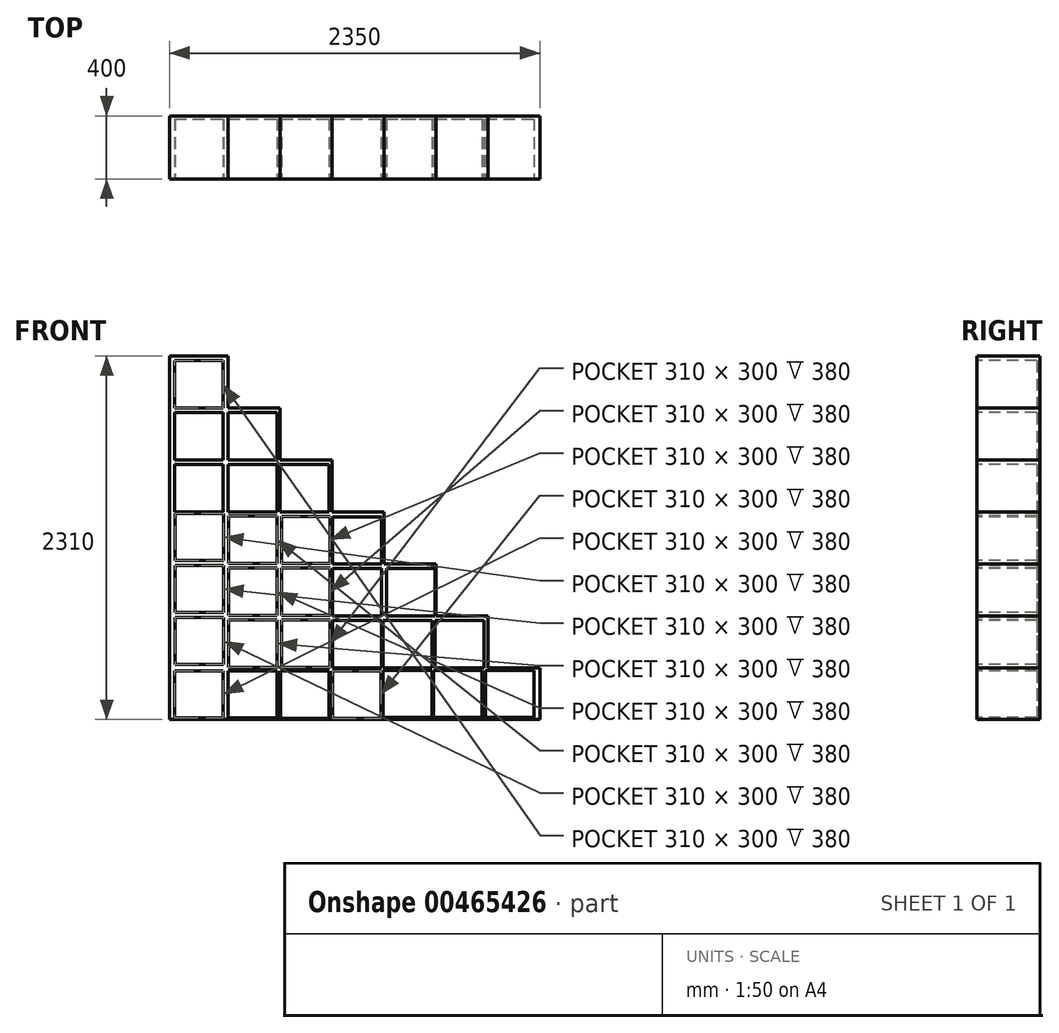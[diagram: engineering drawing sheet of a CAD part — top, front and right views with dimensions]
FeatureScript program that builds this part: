
annotation { "Feature Type Name" : "Feature", "Feature Type Description" : "" }
export const myFeature = defineFeature(function(context is Context, id is Id, definition is map)
    precondition{}
    {
        {
            var Q0;
            Q0=qCreatedBy(makeId("Front.planeOp"),FACE);
            var sketch = newSketch(context, id + "F0", { "sketchPlane" : qUnion([Q0])});
            skLineSegment(sketch, "E0", {"start": v(0, 0) * mm, "end": v(2350, 0) * mm});
            skLineSegment(sketch, "E1", {"start": v(0, 0) * mm, "end": v(0, 2310) * mm});
            skLineSegment(sketch, "E2", {"start": v(2350, 0) * mm, "end": v(2350, 330) * mm});
            skLineSegment(sketch, "E3", {"start": v(2350, 330) * mm, "end": v(2020, 330) * mm});
            skLineSegment(sketch, "E4", {"start": v(2020, 330) * mm, "end": v(2020, 660) * mm});
            skLineSegment(sketch, "E5", {"start": v(2020, 660) * mm, "end": v(1690, 660) * mm});
            skLineSegment(sketch, "E6", {"start": v(1690, 660) * mm, "end": v(1690, 990) * mm});
            skLineSegment(sketch, "E7", {"start": v(1690, 990) * mm, "end": v(1360, 990) * mm});
            skLineSegment(sketch, "E8", {"start": v(1360, 990) * mm, "end": v(1360, 1320) * mm});
            skLineSegment(sketch, "E9", {"start": v(1360, 1320) * mm, "end": v(1030, 1320) * mm});
            skLineSegment(sketch, "E10", {"start": v(1030, 1320) * mm, "end": v(1030, 1650) * mm});
            skLineSegment(sketch, "E11", {"start": v(1030, 1650) * mm, "end": v(700, 1650) * mm});
            skLineSegment(sketch, "E12", {"start": v(700, 1650) * mm, "end": v(700, 1980) * mm});
            skLineSegment(sketch, "E13", {"start": v(700, 1980) * mm, "end": v(370, 1980) * mm});
            skLineSegment(sketch, "E14", {"start": v(370, 1980) * mm, "end": v(370, 2310) * mm});
            skLineSegment(sketch, "E15", {"start": v(370, 2310) * mm, "end": v(0, 2310) * mm});
            skSolve(sketch);
        }
        {
            var Q0;
            Q0=makeQuery(id+"F0.imprint","IMPRINT",FACE,{"disambiguationData":[TD([[makeQuery(id+"F0.imprint","IMPRINT",EDGE,{"derivedFrom":sQuery(id+"F0.wireOp",EDGE,"E0")}),1.0]])]});
            extrude(context, id + "F1", {"entities" : qUnion([Q0]), "depth" : 400 * mm});
        }
        {
            var Q0;
            Q0=makeQuery(id+"F1.opExtrude","CAP_FACE",FACE,{"disambiguationData":[OSD([sQuery(id+"F0.wireOp",EDGE,"E0"),sQuery(id+"F0.wireOp",EDGE,"E1"),sQuery(id+"F0.wireOp",EDGE,"E2"),sQuery(id+"F0.wireOp",EDGE,"E3"),sQuery(id+"F0.wireOp",EDGE,"E4"),sQuery(id+"F0.wireOp",EDGE,"E5"),sQuery(id+"F0.wireOp",EDGE,"E6"),sQuery(id+"F0.wireOp",EDGE,"E7"),sQuery(id+"F0.wireOp",EDGE,"E8"),sQuery(id+"F0.wireOp",EDGE,"E9"),sQuery(id+"F0.wireOp",EDGE,"E10"),sQuery(id+"F0.wireOp",EDGE,"E11"),sQuery(id+"F0.wireOp",EDGE,"E12"),sQuery(id+"F0.wireOp",EDGE,"E13"),sQuery(id+"F0.wireOp",EDGE,"E14"),sQuery(id+"F0.wireOp",EDGE,"E15")])],"isStart":false});
            var sketch = newSketch(context, id + "F2", { "sketchPlane" : qUnion([Q0])});
            skLineSegment(sketch, "E16.bottom", {"start": v(30, 2280) * mm, "end": v(340, 2280) * mm});
            skLineSegment(sketch, "E16.top", {"start": v(30, 1980) * mm, "end": v(340, 1980) * mm});
            skLineSegment(sketch, "E16.left", {"start": v(30, 2280) * mm, "end": v(30, 1980) * mm});
            skLineSegment(sketch, "E16.right", {"start": v(340, 2280) * mm, "end": v(340, 1980) * mm});
            skLineSegment(sketch, "E17.bottom", {"start": v(30, 1950) * mm, "end": v(340, 1950) * mm});
            skLineSegment(sketch, "E17.top", {"start": v(30, 1650) * mm, "end": v(340, 1650) * mm});
            skLineSegment(sketch, "E17.left", {"start": v(30, 1950) * mm, "end": v(30, 1650) * mm});
            skLineSegment(sketch, "E17.right", {"start": v(340, 1950) * mm, "end": v(340, 1650) * mm});
            skLineSegment(sketch, "E18.bottom", {"start": v(370, 1950) * mm, "end": v(680, 1950) * mm});
            skLineSegment(sketch, "E18.top", {"start": v(370, 1650) * mm, "end": v(680, 1650) * mm});
            skLineSegment(sketch, "E18.left", {"start": v(370, 1950) * mm, "end": v(370, 1650) * mm});
            skLineSegment(sketch, "E18.right", {"start": v(680, 1950) * mm, "end": v(680, 1650) * mm});
            skLineSegment(sketch, "E19.bottom", {"start": v(30, 1620) * mm, "end": v(340, 1620) * mm});
            skLineSegment(sketch, "E19.top", {"start": v(30, 1320) * mm, "end": v(340, 1320) * mm});
            skLineSegment(sketch, "E19.left", {"start": v(30, 1620) * mm, "end": v(30, 1320) * mm});
            skLineSegment(sketch, "E19.right", {"start": v(340, 1620) * mm, "end": v(340, 1320) * mm});
            skLineSegment(sketch, "E20.bottom", {"start": v(370, 1620) * mm, "end": v(680, 1620) * mm});
            skLineSegment(sketch, "E20.top", {"start": v(370, 1320) * mm, "end": v(680, 1320) * mm});
            skLineSegment(sketch, "E20.left", {"start": v(370, 1620) * mm, "end": v(370, 1320) * mm});
            skLineSegment(sketch, "E20.right", {"start": v(680, 1620) * mm, "end": v(680, 1320) * mm});
            skLineSegment(sketch, "E21.bottom", {"start": v(700, 1620) * mm, "end": v(1010, 1620) * mm});
            skLineSegment(sketch, "E21.top", {"start": v(700, 1320) * mm, "end": v(1010, 1320) * mm});
            skLineSegment(sketch, "E21.left", {"start": v(700, 1620) * mm, "end": v(700, 1320) * mm});
            skLineSegment(sketch, "E21.right", {"start": v(1010, 1620) * mm, "end": v(1010, 1320) * mm});
            skLineSegment(sketch, "E22.bottom", {"start": v(1035.17, 1288.87) * mm, "end": v(1345.17, 1288.87) * mm});
            skLineSegment(sketch, "E22.top", {"start": v(1035.17, 988.87) * mm, "end": v(1345.17, 988.87) * mm});
            skLineSegment(sketch, "E22.left", {"start": v(1035.17, 1288.87) * mm, "end": v(1035.17, 988.87) * mm});
            skLineSegment(sketch, "E22.right", {"start": v(1345.17, 1288.87) * mm, "end": v(1345.17, 988.87) * mm});
            skLineSegment(sketch, "E23.bottom", {"start": v(1035.17, 958.87) * mm, "end": v(1345.17, 958.87) * mm});
            skLineSegment(sketch, "E23.top", {"start": v(1035.17, 658.87) * mm, "end": v(1345.17, 658.87) * mm});
            skLineSegment(sketch, "E23.left", {"start": v(1035.17, 958.87) * mm, "end": v(1035.17, 658.87) * mm});
            skLineSegment(sketch, "E23.right", {"start": v(1345.17, 958.87) * mm, "end": v(1345.17, 658.87) * mm});
            skLineSegment(sketch, "E24.bottom", {"start": v(1375.17, 958.87) * mm, "end": v(1685.17, 958.87) * mm});
            skLineSegment(sketch, "E24.top", {"start": v(1375.17, 658.87) * mm, "end": v(1685.17, 658.87) * mm});
            skLineSegment(sketch, "E24.left", {"start": v(1375.17, 958.87) * mm, "end": v(1375.17, 658.87) * mm});
            skLineSegment(sketch, "E24.right", {"start": v(1685.17, 958.87) * mm, "end": v(1685.17, 658.87) * mm});
            skLineSegment(sketch, "E25.bottom", {"start": v(1035.17, 628.87) * mm, "end": v(1345.17, 628.87) * mm});
            skLineSegment(sketch, "E25.top", {"start": v(1035.17, 328.87) * mm, "end": v(1345.17, 328.87) * mm});
            skLineSegment(sketch, "E25.left", {"start": v(1035.17, 628.87) * mm, "end": v(1035.17, 328.87) * mm});
            skLineSegment(sketch, "E25.right", {"start": v(1345.17, 628.87) * mm, "end": v(1345.17, 328.87) * mm});
            skLineSegment(sketch, "E26.bottom", {"start": v(1354.72, 628.87) * mm, "end": v(1664.72, 628.87) * mm});
            skLineSegment(sketch, "E26.top", {"start": v(1354.72, 328.87) * mm, "end": v(1664.72, 328.87) * mm});
            skLineSegment(sketch, "E26.left", {"start": v(1354.72, 628.87) * mm, "end": v(1354.72, 328.87) * mm});
            skLineSegment(sketch, "E26.right", {"start": v(1664.72, 628.87) * mm, "end": v(1664.72, 328.87) * mm});
            skLineSegment(sketch, "E27.bottom", {"start": v(1684.72, 628.87) * mm, "end": v(1994.72, 628.87) * mm});
            skLineSegment(sketch, "E27.top", {"start": v(1684.72, 328.87) * mm, "end": v(1994.72, 328.87) * mm});
            skLineSegment(sketch, "E27.left", {"start": v(1684.72, 628.87) * mm, "end": v(1684.72, 328.87) * mm});
            skLineSegment(sketch, "E27.right", {"start": v(1994.72, 628.87) * mm, "end": v(1994.72, 328.87) * mm});
            skLineSegment(sketch, "E28.bottom", {"start": v(1354.54, 313.12) * mm, "end": v(1664.54, 313.12) * mm});
            skLineSegment(sketch, "E28.top", {"start": v(1354.54, 13.12) * mm, "end": v(1664.54, 13.12) * mm});
            skLineSegment(sketch, "E28.left", {"start": v(1354.54, 313.12) * mm, "end": v(1354.54, 13.12) * mm});
            skLineSegment(sketch, "E28.right", {"start": v(1664.54, 313.12) * mm, "end": v(1664.54, 13.12) * mm});
            skLineSegment(sketch, "E29.bottom", {"start": v(1674.08, 313.12) * mm, "end": v(1984.08, 313.12) * mm});
            skLineSegment(sketch, "E29.top", {"start": v(1674.08, 13.12) * mm, "end": v(1984.08, 13.12) * mm});
            skLineSegment(sketch, "E29.left", {"start": v(1674.08, 313.12) * mm, "end": v(1674.08, 13.12) * mm});
            skLineSegment(sketch, "E29.right", {"start": v(1984.08, 313.12) * mm, "end": v(1984.08, 13.12) * mm});
            skLineSegment(sketch, "E30.bottom", {"start": v(2004.08, 313.12) * mm, "end": v(2314.08, 313.12) * mm});
            skLineSegment(sketch, "E30.top", {"start": v(2004.08, 13.12) * mm, "end": v(2314.08, 13.12) * mm});
            skLineSegment(sketch, "E30.left", {"start": v(2004.08, 313.12) * mm, "end": v(2004.08, 13.12) * mm});
            skLineSegment(sketch, "E30.right", {"start": v(2314.08, 313.12) * mm, "end": v(2314.08, 13.12) * mm});
            skLineSegment(sketch, "E31.bottom", {"start": v(370, 310.84) * mm, "end": v(680, 310.84) * mm});
            skLineSegment(sketch, "E31.top", {"start": v(370, 10.84) * mm, "end": v(680, 10.84) * mm});
            skLineSegment(sketch, "E31.left", {"start": v(370, 310.84) * mm, "end": v(370, 10.84) * mm});
            skLineSegment(sketch, "E31.right", {"start": v(680, 310.84) * mm, "end": v(680, 10.84) * mm});
            skLineSegment(sketch, "E32.bottom", {"start": v(702.77, 308.71) * mm, "end": v(1012.77, 308.71) * mm});
            skLineSegment(sketch, "E32.top", {"start": v(702.77, 8.71) * mm, "end": v(1012.77, 8.71) * mm});
            skLineSegment(sketch, "E32.left", {"start": v(702.77, 308.71) * mm, "end": v(702.77, 8.71) * mm});
            skLineSegment(sketch, "E32.right", {"start": v(1012.77, 308.71) * mm, "end": v(1012.77, 8.71) * mm});
            skLineSegment(sketch, "E33.bottom", {"start": v(1032.77, 308.71) * mm, "end": v(1342.77, 308.71) * mm});
            skLineSegment(sketch, "E33.top", {"start": v(1032.77, 8.71) * mm, "end": v(1342.77, 8.71) * mm});
            skLineSegment(sketch, "E33.left", {"start": v(1032.77, 308.71) * mm, "end": v(1032.77, 8.71) * mm});
            skLineSegment(sketch, "E33.right", {"start": v(1342.77, 308.71) * mm, "end": v(1342.77, 8.71) * mm});
            skLineSegment(sketch, "E34.bottom", {"start": v(30, 310.5) * mm, "end": v(340, 310.5) * mm});
            skLineSegment(sketch, "E34.top", {"start": v(30, 10.5) * mm, "end": v(340, 10.5) * mm});
            skLineSegment(sketch, "E34.left", {"start": v(30, 310.5) * mm, "end": v(30, 10.5) * mm});
            skLineSegment(sketch, "E34.right", {"start": v(340, 310.5) * mm, "end": v(340, 10.5) * mm});
            skLineSegment(sketch, "E35.bottom", {"start": v(32.4, 1310.15) * mm, "end": v(342.4, 1310.15) * mm});
            skLineSegment(sketch, "E35.top", {"start": v(32.4, 1010.15) * mm, "end": v(342.4, 1010.15) * mm});
            skLineSegment(sketch, "E35.left", {"start": v(32.4, 1310.15) * mm, "end": v(32.4, 1010.15) * mm});
            skLineSegment(sketch, "E35.right", {"start": v(342.4, 1310.15) * mm, "end": v(342.4, 1010.15) * mm});
            skLineSegment(sketch, "E36.bottom", {"start": v(32.4, 980.15) * mm, "end": v(342.4, 980.15) * mm});
            skLineSegment(sketch, "E36.top", {"start": v(32.4, 680.15) * mm, "end": v(342.4, 680.15) * mm});
            skLineSegment(sketch, "E36.left", {"start": v(32.4, 980.15) * mm, "end": v(32.4, 680.15) * mm});
            skLineSegment(sketch, "E36.right", {"start": v(342.4, 980.15) * mm, "end": v(342.4, 680.15) * mm});
            skLineSegment(sketch, "E37.bottom", {"start": v(32.4, 650.15) * mm, "end": v(342.4, 650.15) * mm});
            skLineSegment(sketch, "E37.top", {"start": v(32.4, 350.15) * mm, "end": v(342.4, 350.15) * mm});
            skLineSegment(sketch, "E37.left", {"start": v(32.4, 650.15) * mm, "end": v(32.4, 350.15) * mm});
            skLineSegment(sketch, "E37.right", {"start": v(342.4, 650.15) * mm, "end": v(342.4, 350.15) * mm});
            skLineSegment(sketch, "E38.bottom", {"start": v(372.4, 1293.28) * mm, "end": v(682.4, 1293.28) * mm});
            skLineSegment(sketch, "E38.top", {"start": v(372.4, 993.28) * mm, "end": v(682.4, 993.28) * mm});
            skLineSegment(sketch, "E38.left", {"start": v(372.4, 1293.28) * mm, "end": v(372.4, 993.28) * mm});
            skLineSegment(sketch, "E38.right", {"start": v(682.4, 1293.28) * mm, "end": v(682.4, 993.28) * mm});
            skLineSegment(sketch, "E39.bottom", {"start": v(372.4, 963.28) * mm, "end": v(682.4, 963.28) * mm});
            skLineSegment(sketch, "E39.top", {"start": v(372.4, 663.28) * mm, "end": v(682.4, 663.28) * mm});
            skLineSegment(sketch, "E39.left", {"start": v(372.4, 963.28) * mm, "end": v(372.4, 663.28) * mm});
            skLineSegment(sketch, "E39.right", {"start": v(682.4, 963.28) * mm, "end": v(682.4, 663.28) * mm});
            skLineSegment(sketch, "E40.bottom", {"start": v(372.4, 633.28) * mm, "end": v(682.4, 633.28) * mm});
            skLineSegment(sketch, "E40.top", {"start": v(372.4, 333.28) * mm, "end": v(682.4, 333.28) * mm});
            skLineSegment(sketch, "E40.left", {"start": v(372.4, 633.28) * mm, "end": v(372.4, 333.28) * mm});
            skLineSegment(sketch, "E40.right", {"start": v(682.4, 633.28) * mm, "end": v(682.4, 333.28) * mm});
            skLineSegment(sketch, "E41.bottom", {"start": v(708.6, 1292.06) * mm, "end": v(1018.6, 1292.06) * mm});
            skLineSegment(sketch, "E41.top", {"start": v(708.6, 992.06) * mm, "end": v(1018.6, 992.06) * mm});
            skLineSegment(sketch, "E41.left", {"start": v(708.6, 1292.06) * mm, "end": v(708.6, 992.06) * mm});
            skLineSegment(sketch, "E41.right", {"start": v(1018.6, 1292.06) * mm, "end": v(1018.6, 992.06) * mm});
            skLineSegment(sketch, "E42.bottom", {"start": v(708.6, 962.06) * mm, "end": v(1018.6, 962.06) * mm});
            skLineSegment(sketch, "E42.top", {"start": v(708.6, 662.06) * mm, "end": v(1018.6, 662.06) * mm});
            skLineSegment(sketch, "E42.left", {"start": v(708.6, 962.06) * mm, "end": v(708.6, 662.06) * mm});
            skLineSegment(sketch, "E42.right", {"start": v(1018.6, 962.06) * mm, "end": v(1018.6, 662.06) * mm});
            skLineSegment(sketch, "E43.bottom", {"start": v(708.6, 632.06) * mm, "end": v(1018.6, 632.06) * mm});
            skLineSegment(sketch, "E43.top", {"start": v(708.6, 332.06) * mm, "end": v(1018.6, 332.06) * mm});
            skLineSegment(sketch, "E43.left", {"start": v(708.6, 632.06) * mm, "end": v(708.6, 332.06) * mm});
            skLineSegment(sketch, "E43.right", {"start": v(1018.6, 632.06) * mm, "end": v(1018.6, 332.06) * mm});
            skSolve(sketch);
        }
        {
            var Q0;
            Q0 = qSketchRegion(id + "F2", true);
            extrude(context, id + "F3", {"entities" : qUnion([Q0]), "operationType" : NewBodyOperationType.REMOVE, "oppositeDirection" : true, "depth" : 380 * mm});
        }
    });
